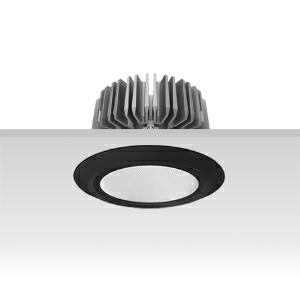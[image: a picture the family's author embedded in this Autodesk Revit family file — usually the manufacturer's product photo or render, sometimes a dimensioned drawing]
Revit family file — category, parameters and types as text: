
# Revit family: 3f_filippi_-_3f_reno_bianco_ampio_3f_filippi_-_30353_a01047_-_3f_reno_150_wh_3000-930_wide___smp_bk_1c2e
name_source: partatom
category: Lighting Fixtures
units: mm (PartAtom-declared; Revit-internal decimal feet)

## family parameters
Cut with Voids When Loaded = No
Host = Face
Light Source = No
Part Type = Normal
Room Calculation Point = No
Round Connector Dimension = Use Diameter
Shared = No

## types (1)
- 3F Filippi - 3F Reno Bianco Ampio (1 x LED, 2324 lm, 37 W, 3000 K)
    Apparent Load = 37 VA
    Approval mark = CE
    CIE Flux Codes = 73 92 98 100 100
    Color Rendering = 90
    Color Temperature = 3000 K
    Control Gear = Electronic ballast
    Default Elevation = 1800 mm
    Description = ILLUMINOTECHNICAL
Luminous efficiency 100% (DLOR 100%, ULOR 0%).
Initial luminous flux of the luminaire 2324 lm.
Direct symmetric wide distribution.
Installation Interdistance Transv.D = 1.01 x hu - Long.D = 1.00 x hu.
Tabular UGR (CIE 117 - 4H-8H; S=0.25H; 70/50/20): RUG 24.5 - 24.5.
Beam angle: 70° - 70°.
Luminous efficacy 63 lm/W.
Lifetime (L90/B10): 30000 h. (tq+25°C)
Lifetime (L85/B10): 50000 h. (tq+25°C)
Lifetime (L70/B10): 80000 h. (tq+25°C)
Sudden decreased luminous flux after 50000 hours: 0% (C0).
Photobiological safety in compliance with IEC/TR 62778: RG0 risk exempt, (IEC 62471).
In compliance with IEC/EN 62722-2-1 - IEC/EN 62717 standards.

SOURCE
Compact LED module 3000/930.
Energy efficiency class (UE 2019/2020 - UE 2019/2015): E.
CIE 13.3 Colour rendering index: CRI >90 (R9 >50%).
IES TM-30 Fidelity Index: Rf = 92 Rg = 101.
CCT nominal colour temperature 3000 K.
Colour initial tolerance (MacAdam): SDCM 3.
Zhaga Book 3 compliant.

MECHANICAL
Passive heat dissipator in die-casting aluminium, oversized, for optimum thermal management of the LED module.
Parabolic element with graduated/concentric rings in white polycarbonate.
Transparent external lens with glossy and satin differentiated surfaces, with a cooling and anti-insect system in methacrylate (PMMA).
Fastening spring clips in stainless steel.
Dimensions: diameter 176 mm, height 111 mm. Weight 1.395 kg.
IP44 protection degree for exposed part, IP20 for recessed part.
Mechanical strength to impacts IK05 (0.7 joule).
Glow-wire test resistance 650°C.

ELECTRICAL
Wiring on a separate unit.
Halogen Free electronic wiring 230V-50/60Hz, power factor 0.95, THD <25%, constant output current, SELV, class II, 1 driver.
Power of the luminaire 37 W.
ENEC - CE.
SAFE FLICKER: PstLM=<1 and SVM=<0.4 (IEC TR 61547-1 and IEC TR 63158), to ensure a more comfortable and safe light.
Luminaire compliant with EN 60598-2-22 for power supply from a centralised emergency system CPSS (Central Power Supply System), not incorporated in the luminaire - high risk areas excluded. The default power and flux are 100% in AC and 100% in DC.
Ambient temperature from 0°C to +25°C.
Temperature class T6 max 85°C.
Relative humidity UR: <85%.

INSTALLATION
Pull-up recessed fitting.
False ceiling carving: 150 mm.
All accessories dedicated to this product are available on the Catalog and on our website www.3F-Filippi.com.

ACCESSORIES
A01047 - Anti-glare microprismatic SMP diffuser in methacrylate (PMMA), locked and in line with the trim, in black polycarbonate.

APPLICATIONS
Suitable product for food production plants (HACCP), IFS (Food Version 6), BRC (GSFS Food Version 7).
Environments: architectural, commercial, exhibition areas, transit areas, corridors, shops, display windows, service areas.
In false ceilings with narrow voids.

WARNING
Luminaire designed for disposal/recycling at end-of-life.
Replaceable (LED only) light source by a professional. Replaceable control gear by a professional.
    Height = 0 mm  [stored 0 ft]
    Lamp = 1 x LED
    Lamp Light Flux = 2324 lm
    Lamp Power = 37 W
    Lamp count = 1
    Length = 176 mm
    Lifetime = 50000 h
    Luminous efficacy = 63 lm/W
    Manufacturer = 3F Filippi
    ModVariant = No
    Model = 3F Filippi - 30353+A01047 - 3F Reno 150 WH 3000-930 WIDE + SMP BK
    Mounting Place = Ceiling
    Mounting Type = Recessed
    Number of Poles = 1
    OnlyDefault = Yes
    Power Factor = 1
    Product Name = 3F Filippi - 3F Reno Bianco Ampio
    Product group = recessed luminaire
    ProductGroupID = 4
    Protection Class = Protection class II
    Protection Degree = IP 20
    RLX_Detail_Level = 1
    RLX_Emergency_Light_Flux = 0 lm
    RLX_Emergency_Type = 0
    RLX_Emergency_Type_DB = No
    RlxData = <blob elided: 85861 chars, md5=308f913a>
    Socket = socket
    Standby Power = 0 W
    System Light Flux = 2324 lm
    System Power = 37 W
    Type Comments = Product without accessories
    Type Image = 3ffilippi_3f_reno_150_bk_vs_smp.jpg
    URL = http://relux.com
    VarID = ---
    Voltage = 0 V
    Weight = 0.00 kg
    Width = 0 mm  [stored 0 ft]

note: [stored X ft] marks values corroborated as IEEE doubles in the binary element streams (Revit-internal decimal feet)

## geometry (parser evidence)
native form markers: Blend x4, Sweep x11
no freeform markers — native parametric forms only
